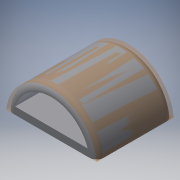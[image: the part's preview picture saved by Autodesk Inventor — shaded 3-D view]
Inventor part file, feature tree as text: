
AUTODESK INVENTOR PART (.ipt)
format: ipt  version: 2019 (Build 230136000, 136)  size: 131,072 bytes
history: native  units: mm
features: thicken_offset x1, fillet x1, sketch x1, other x1, extrude x1
ambient origin geometry x8: Origin, YZ Plane, XZ Plane, XY Plane, X Axis, Y Axis, Z Axis, Center Point
bodies: Solid1 (feature_tree)
feature tree (5):
  thicken_offset  "Thicken1"
  fillet  "Fillet1"  Radius=100.0mm
  sketch  "Sketch1"  dims[d1=5.0mm d2=85.0mm d3=0.0mm d4=8.0mm d5=8.0mm d6=8.0mm]
  other  "Srf1"
  extrude  "ExtrusionSrf1"  Depth=8.0mm TaperAngle=0.0deg
